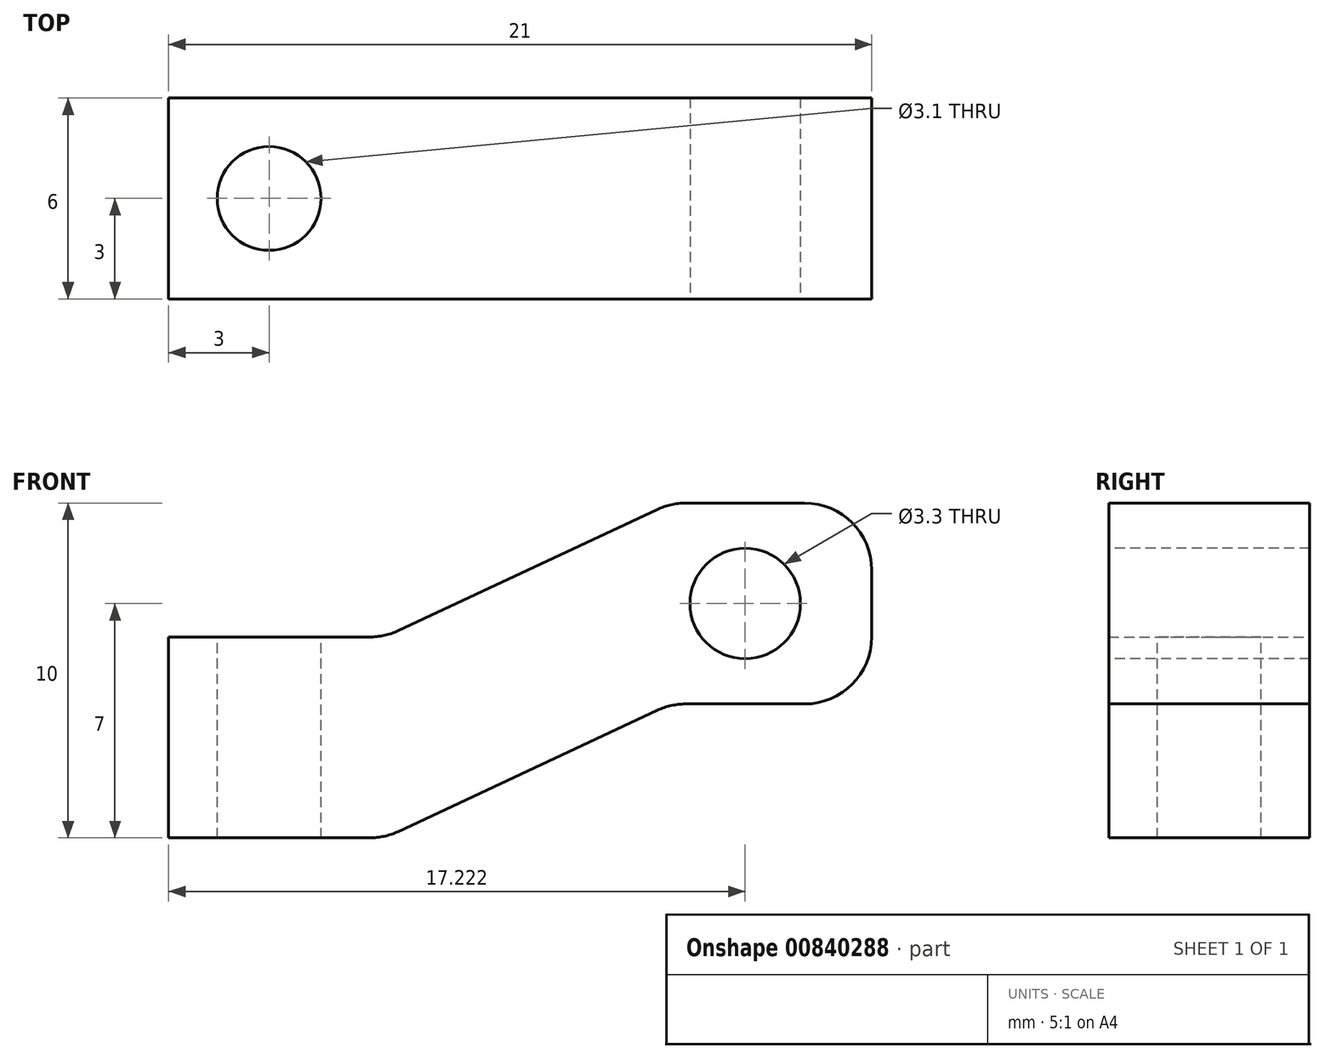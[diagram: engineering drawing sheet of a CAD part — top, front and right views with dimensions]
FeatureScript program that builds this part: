
annotation { "Feature Type Name" : "Feature", "Feature Type Description" : "" }
export const myFeature = defineFeature(function(context is Context, id is Id, definition is map)
    precondition{}
    {
        {
            var Q0;
            Q0=qCreatedBy(makeId("Front.planeOp"),FACE);
            var sketch = newSketch(context, id + "F0", { "sketchPlane" : qUnion([Q0])});
            skLineSegment(sketch, "E0", {"start": v(0, 0) * mm, "end": v(6, 0) * mm});
            skLineSegment(sketch, "E1", {"start": v(6.85, 0.19) * mm, "end": v(14.6, 3.81) * mm});
            skLineSegment(sketch, "E2", {"start": v(15.44, 4) * mm, "end": v(19, 4) * mm});
            skLineSegment(sketch, "E3", {"start": v(21, 6) * mm, "end": v(21, 8) * mm});
            skLineSegment(sketch, "E4", {"start": v(19, 10) * mm, "end": v(15.44, 10) * mm});
            skLineSegment(sketch, "E5", {"start": v(14.6, 9.81) * mm, "end": v(6.85, 6.19) * mm});
            skLineSegment(sketch, "E6", {"start": v(6, 6) * mm, "end": v(0, 6) * mm});
            skLineSegment(sketch, "E7", {"start": v(0, 6) * mm, "end": v(0, 0) * mm});
            skPoint(sketch, "E8.visualSharp", {"position": v(21, 10) * mm});
            skArc(sketch, "E8.filletArc", {"start": v(21, 8) * mm, "mid": v(20.41, 9.41) * mm, "end": v(19, 10) * mm});
            skPoint(sketch, "E9.visualSharp", {"position": v(21, 4) * mm});
            skArc(sketch, "E9.filletArc", {"start": v(19, 4) * mm, "mid": v(20.41, 4.59) * mm, "end": v(21, 6) * mm});
            skPoint(sketch, "E10.visualSharp", {"position": v(15, 4) * mm});
            skArc(sketch, "E10.filletArc", {"start": v(15.44, 4) * mm, "mid": v(15.01, 3.95) * mm, "end": v(14.6, 3.81) * mm});
            skPoint(sketch, "E11.visualSharp", {"position": v(15, 10) * mm});
            skArc(sketch, "E11.filletArc", {"start": v(15.44, 10) * mm, "mid": v(15.01, 9.95) * mm, "end": v(14.6, 9.81) * mm});
            skPoint(sketch, "E12.visualSharp", {"position": v(6.44, 6) * mm});
            skArc(sketch, "E12.filletArc", {"start": v(6, 6) * mm, "mid": v(6.43, 6.05) * mm, "end": v(6.85, 6.19) * mm});
            skPoint(sketch, "E13.visualSharp", {"position": v(6.44, 0) * mm});
            skArc(sketch, "E13.filletArc", {"start": v(6, 0) * mm, "mid": v(6.43, 0.05) * mm, "end": v(6.85, 0.19) * mm});
            skLineSegment(sketch, "E14", {"start": v(19, 10) * mm, "end": v(19, 4) * mm, "construction": true});
            skSolve(sketch);
        }
        {
            var Q0;
            Q0 = qSketchRegion(id + "F0", true);
            extrude(context, id + "F1", {"entities" : qUnion([Q0]), "depth" : 6 * mm, "offsetDistance" : 25 * mm});
        }
        {
            var Q0;
            Q0=makeQuery(id+"F1.opExtrude","SWEPT_FACE",FACE,{"disambiguationData":[OSD([sQuery(id+"F0.wireOp",EDGE,"E6")])]});
            var sketch = newSketch(context, id + "F2", { "sketchPlane" : qUnion([Q0])});
            skLineSegment(sketch, "E15", {"start": v(0, -6) * mm, "end": v(6, 0) * mm, "construction": true});
            skCircle(sketch, "E16", {"center": v(3, -3) * mm, "radius": 1.55 * mm});
            skSolve(sketch);
        }
        {
            var Q0;
            Q0 = qSketchRegion(id + "F2", true);
            extrude(context, id + "F3", {"entities" : qUnion([Q0]), "operationType" : NewBodyOperationType.REMOVE, "endBound" : BoundingType.UP_TO_NEXT, "oppositeDirection" : true, "depth" : 25 * mm, "offsetDistance" : 25 * mm});
        }
        {
            var Q0;
            Q0=makeQuery(id+"F1.opExtrude","CAP_FACE",FACE,{"disambiguationData":[OSD([sQuery(id+"F0.wireOp",EDGE,"E0"),sQuery(id+"F0.wireOp",EDGE,"E1"),sQuery(id+"F0.wireOp",EDGE,"E2"),sQuery(id+"F0.wireOp",EDGE,"E3"),sQuery(id+"F0.wireOp",EDGE,"E4"),sQuery(id+"F0.wireOp",EDGE,"E5"),sQuery(id+"F0.wireOp",EDGE,"E6"),sQuery(id+"F0.wireOp",EDGE,"E7"),sQuery(id+"F0.wireOp",EDGE,"E8.filletArc"),sQuery(id+"F0.wireOp",EDGE,"E9.filletArc"),sQuery(id+"F0.wireOp",EDGE,"E10.filletArc"),sQuery(id+"F0.wireOp",EDGE,"E11.filletArc"),sQuery(id+"F0.wireOp",EDGE,"E12.filletArc"),sQuery(id+"F0.wireOp",EDGE,"E13.filletArc")])],"isStart":false});
            var sketch = newSketch(context, id + "F4", { "sketchPlane" : qUnion([Q0])});
            skLineSegment(sketch, "E17", {"start": v(19, 10) * mm, "end": v(15.44, 4) * mm, "construction": true});
            skCircle(sketch, "E18", {"center": v(17.22, 7) * mm, "radius": 1.65 * mm});
            skSolve(sketch);
        }
        {
            var Q0;
            Q0 = qSketchRegion(id + "F4", true);
            extrude(context, id + "F5", {"entities" : qUnion([Q0]), "operationType" : NewBodyOperationType.REMOVE, "endBound" : BoundingType.UP_TO_NEXT, "oppositeDirection" : true, "depth" : 25 * mm, "offsetDistance" : 25 * mm});
        }
    });
